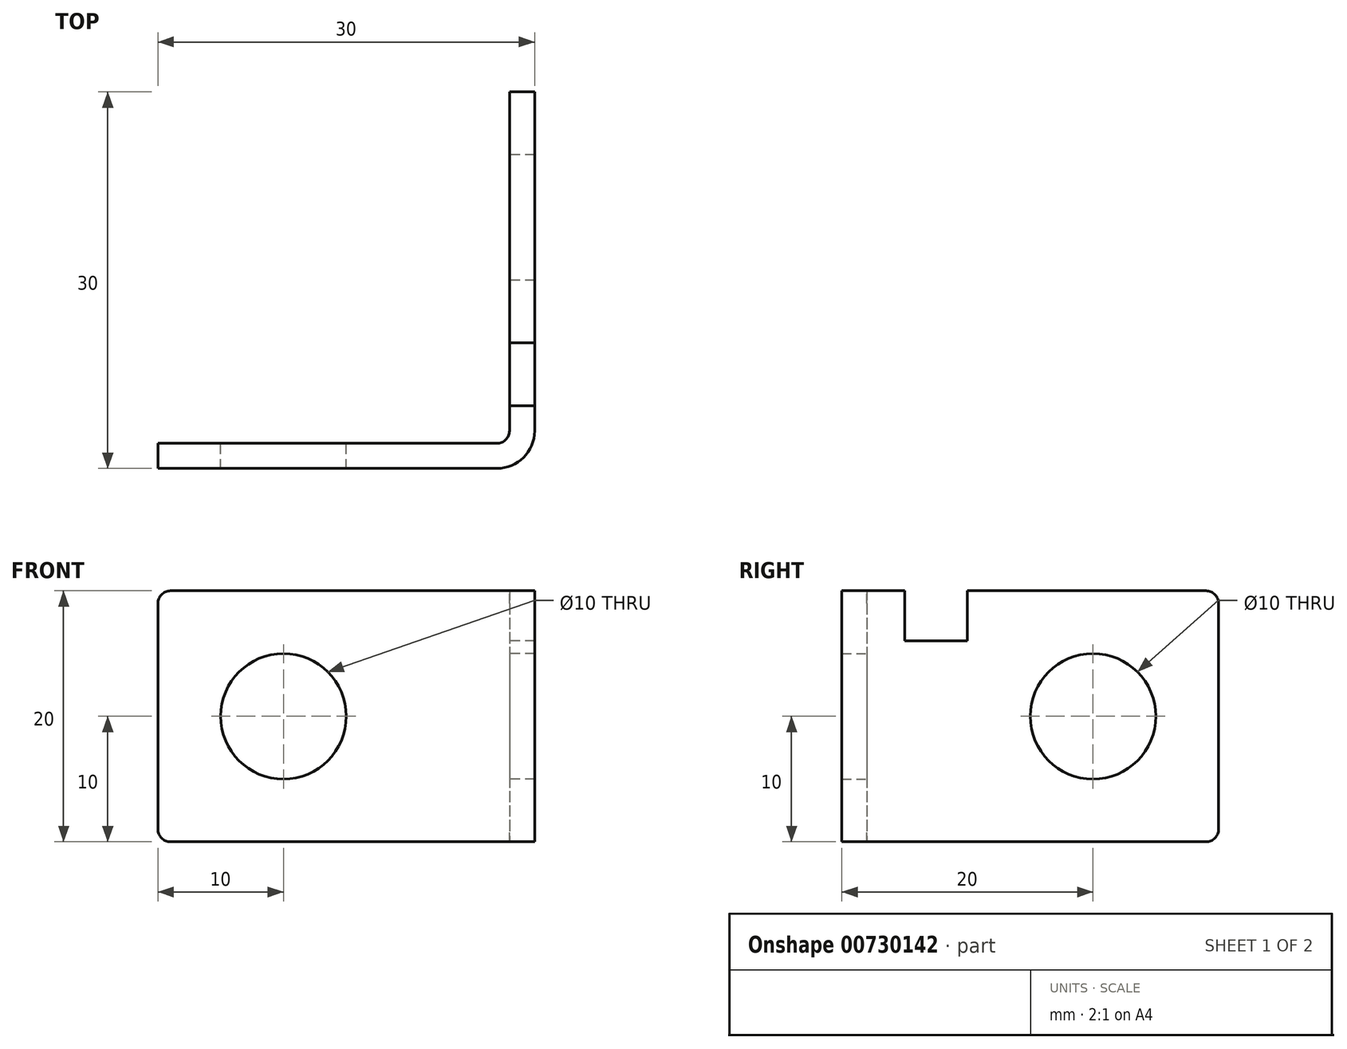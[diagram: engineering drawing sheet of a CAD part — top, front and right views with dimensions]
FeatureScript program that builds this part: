
annotation { "Feature Type Name" : "Feature", "Feature Type Description" : "" }
export const myFeature = defineFeature(function(context is Context, id is Id, definition is map)
    precondition{}
    {
        {
            var Q0;
            Q0=qCreatedBy(makeId("Top.planeOp"),FACE);
            var sketch = newSketch(context, id + "F0", { "sketchPlane" : qUnion([Q0])});
            skLineSegment(sketch, "E0.bottom", {"start": v(0, 0) * mm, "end": v(30, 0) * mm});
            skLineSegment(sketch, "E0.top", {"start": v(0, 2) * mm, "end": v(28, 2) * mm});
            skLineSegment(sketch, "E0.left", {"start": v(0, 0) * mm, "end": v(0, 2) * mm});
            skLineSegment(sketch, "E1", {"start": v(30, 30) * mm, "end": v(28, 30) * mm});
            skLineSegment(sketch, "E2", {"start": v(28, 30) * mm, "end": v(28, 2) * mm});
            skLineSegment(sketch, "E3", {"start": v(30, 30) * mm, "end": v(30, 0) * mm});
            skSolve(sketch);
        }
        {
            var Q0;
            Q0 = qSketchRegion(id + "F0", true);
            extrude(context, id + "F1", {"entities" : qUnion([Q0]), "depth" : 20 * mm, "offsetDistance" : 25 * mm});
        }
        {
            var Q0;
            Q0=makeQuery(id+"F1.opExtrude","SWEPT_EDGE",EDGE,{"disambiguationData":[OSD([sQuery(id+"F0.wireOp",EDGE,"E0.top"),sQuery(id+"F0.wireOp",EDGE,"E2")])]});
            var Q1;
            Q1=makeQuery(id+"F1.opExtrude","CAP_EDGE",EDGE,{"disambiguationData":[OSD([sQuery(id+"F0.wireOp",EDGE,"E0.left")])],"isStart":true});
            var Q2;
            Q2=makeQuery(id+"F1.opExtrude","CAP_EDGE",EDGE,{"disambiguationData":[OSD([sQuery(id+"F0.wireOp",EDGE,"E0.left")])],"isStart":false});
            var Q3;
            Q3=makeQuery(id+"F1.opExtrude","CAP_EDGE",EDGE,{"disambiguationData":[OSD([sQuery(id+"F0.wireOp",EDGE,"E1")])],"isStart":false});
            var Q4;
            Q4=makeQuery(id+"F1.opExtrude","CAP_EDGE",EDGE,{"disambiguationData":[OSD([sQuery(id+"F0.wireOp",EDGE,"E1")])],"isStart":true});
            fillet(context, id + "F2", {"entities" : qUnion([Q0, Q1, Q2, Q3, Q4]), "radius" : 1 * mm, "tangentPropagation" : true, "allowEdgeOverflow" : false});
        }
        {
            var Q0;
            Q0=makeQuery(id+"F1.opExtrude","SWEPT_EDGE",EDGE,{"disambiguationData":[OSD([sQuery(id+"F0.wireOp",EDGE,"E0.bottom"),sQuery(id+"F0.wireOp",EDGE,"E3")])]});
            fillet(context, id + "F3", {"entities" : qUnion([Q0]), "radius" : 3 * mm, "tangentPropagation" : true, "allowEdgeOverflow" : false});
        }
        {
            var Q0;
            Q0=makeQuery(id+"F1.opExtrude","SWEPT_FACE",FACE,{"disambiguationData":[OSD([sQuery(id+"F0.wireOp",EDGE,"E2")])]});
            var sketch = newSketch(context, id + "F4", { "sketchPlane" : qUnion([Q0])});
            skCircle(sketch, "E4", {"center": v(-20, 10) * mm, "radius": 5 * mm});
            skSolve(sketch);
        }
        {
            var Q0;
            Q0=makeQuery(id+"F4.imprint","IMPRINT",FACE,{"disambiguationData":[TD([[makeQuery(id+"F4.imprint","IMPRINT",EDGE,{"derivedFrom":sQuery(id+"F4.wireOp",EDGE,"E4")}),1.0]])]});
            extrude(context, id + "F5", {"entities" : qUnion([Q0]), "operationType" : NewBodyOperationType.REMOVE, "oppositeDirection" : true, "depth" : 25 * mm, "offsetDistance" : 25 * mm});
        }
        {
            var Q0;
            Q0=makeQuery(id+"F1.opExtrude","SWEPT_FACE",FACE,{"disambiguationData":[OSD([sQuery(id+"F0.wireOp",EDGE,"E0.top")])]});
            var sketch = newSketch(context, id + "F6", { "sketchPlane" : qUnion([Q0])});
            skCircle(sketch, "E5", {"center": v(-10, 10) * mm, "radius": 5 * mm});
            skSolve(sketch);
        }
        {
            var Q0;
            Q0=makeQuery(id+"F6.imprint","IMPRINT",FACE,{"disambiguationData":[TD([[makeQuery(id+"F6.imprint","IMPRINT",EDGE,{"derivedFrom":sQuery(id+"F6.wireOp",EDGE,"E5")}),1.0]])]});
            extrude(context, id + "F7", {"entities" : qUnion([Q0]), "operationType" : NewBodyOperationType.REMOVE, "oppositeDirection" : true, "depth" : 25 * mm, "offsetDistance" : 25 * mm});
        }
        {
            var Q0;
            Q0=makeQuery(id+"F1.opExtrude","SWEPT_FACE",FACE,{"disambiguationData":[OSD([sQuery(id+"F0.wireOp",EDGE,"E2")])]});
            var sketch = newSketch(context, id + "F8", { "sketchPlane" : qUnion([Q0])});
            skLineSegment(sketch, "E6.bottom", {"start": v(-10, 20) * mm, "end": v(-5, 20) * mm});
            skLineSegment(sketch, "E6.top", {"start": v(-10, 16) * mm, "end": v(-5, 16) * mm});
            skLineSegment(sketch, "E6.left", {"start": v(-10, 20) * mm, "end": v(-10, 16) * mm});
            skLineSegment(sketch, "E6.right", {"start": v(-5, 20) * mm, "end": v(-5, 16) * mm});
            skSolve(sketch);
        }
        {
            var Q0;
            Q0=makeQuery(id+"F8.imprint","IMPRINT",FACE,{"disambiguationData":[TD([[makeQuery(id+"F8.imprint","IMPRINT",EDGE,{"derivedFrom":sQuery(id+"F8.wireOp",EDGE,"E6.bottom")}),-1.0]])]});
            extrude(context, id + "F9", {"entities" : qUnion([Q0]), "operationType" : NewBodyOperationType.REMOVE, "oppositeDirection" : true, "depth" : 25 * mm, "offsetDistance" : 25 * mm});
        }
    });
